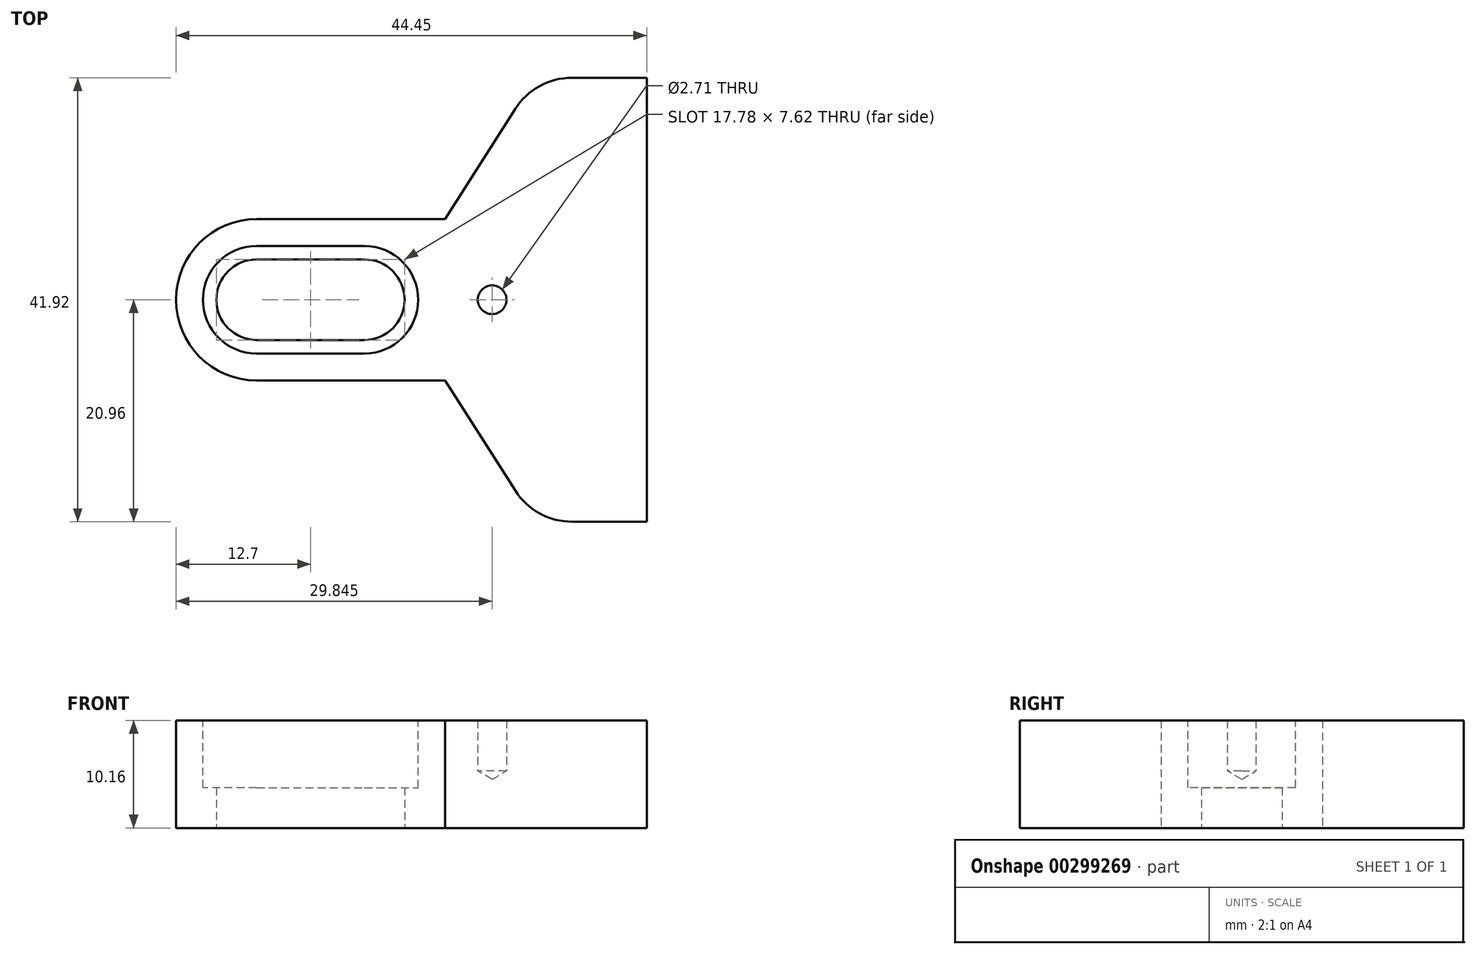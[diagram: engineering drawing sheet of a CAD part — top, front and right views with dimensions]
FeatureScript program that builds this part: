
annotation { "Feature Type Name" : "Feature", "Feature Type Description" : "" }
export const myFeature = defineFeature(function(context is Context, id is Id, definition is map)
    precondition{}
    {
        {
            var Q0;
            Q0=qCreatedBy(makeId("Top.planeOp"),FACE);
            var sketch = newSketch(context, id + "F0", { "sketchPlane" : qUnion([Q0])});
            skLineSegment(sketch, "E0.bottom", {"start": v(7.62, 7.62) * mm, "end": v(25.4, 7.62) * mm});
            skLineSegment(sketch, "E0.top", {"start": v(7.62, -7.62) * mm, "end": v(25.4, -7.62) * mm});
            skLineSegment(sketch, "E1", {"start": v(0, 0) * mm, "end": v(44.45, 0) * mm, "construction": true});
            skArc(sketch, "E2", {"start": v(7.62, 7.62) * mm, "mid": v(0, 0) * mm, "end": v(7.62, -7.62) * mm});
            skPoint(sketch, "E3.orphan", {"position": v(0, 7.62) * mm});
            skPoint(sketch, "E4.orphan", {"position": v(0, -7.62) * mm});
            skLineSegment(sketch, "E5", {"start": v(32.02, 18.02) * mm, "end": v(25.4, 7.62) * mm});
            skLineSegment(sketch, "E6", {"start": v(25.4, -7.62) * mm, "end": v(32.02, -18.02) * mm});
            skPoint(sketch, "E7.visualSharp", {"position": v(20.55, 0) * mm});
            skArc(sketch, "E8.filletArc", {"start": v(37.38, 20.96) * mm, "mid": v(34.32, 20.17) * mm, "end": v(32.02, 18.02) * mm});
            skArc(sketch, "E9.filletArc", {"start": v(32.02, -18.02) * mm, "mid": v(34.32, -20.17) * mm, "end": v(37.38, -20.96) * mm});
            skLineSegment(sketch, "E10", {"start": v(37.38, 20.96) * mm, "end": v(44.45, 20.96) * mm});
            skLineSegment(sketch, "E11", {"start": v(44.45, 20.96) * mm, "end": v(44.45, -20.96) * mm});
            skLineSegment(sketch, "E12", {"start": v(44.45, -20.96) * mm, "end": v(37.38, -20.96) * mm});
            skPoint(sketch, "E13.orphan", {"position": v(24.86, -6.78) * mm});
            skPoint(sketch, "E14.orphan", {"position": v(24.86, 6.78) * mm});
            skLineSegment(sketch, "E15", {"start": v(25.4, 7.62) * mm, "end": v(25.4, -7.62) * mm, "construction": true});
            skSolve(sketch);
        }
        {
            var Q0;
            Q0 = qSketchRegion(id + "F0", true);
            extrude(context, id + "F1", {"entities" : qUnion([Q0]), "depth" : 10.16 * mm});
        }
        {
            var Q0;
            Q0=makeQuery(id+"F1.opExtrude","CAP_FACE",FACE,{"disambiguationData":[OSD([sQuery(id+"F0.wireOp",EDGE,"E0.bottom"),sQuery(id+"F0.wireOp",EDGE,"E0.top"),sQuery(id+"F0.wireOp",EDGE,"E2"),sQuery(id+"F0.wireOp",EDGE,"E5"),sQuery(id+"F0.wireOp",EDGE,"E6"),sQuery(id+"F0.wireOp",EDGE,"E8.filletArc"),sQuery(id+"F0.wireOp",EDGE,"E9.filletArc"),sQuery(id+"F0.wireOp",EDGE,"E10"),sQuery(id+"F0.wireOp",EDGE,"E11"),sQuery(id+"F0.wireOp",EDGE,"E12")])],"isStart":false});
            var sketch = newSketch(context, id + "F2", { "sketchPlane" : qUnion([Q0])});
            skLineSegment(sketch, "E16", {"start": v(7.62, 0) * mm, "end": v(17.78, 0) * mm});
            skArc(sketch, "E17.0.startCap", {"start": v(7.62, -5.08) * mm, "mid": v(2.54, 0) * mm, "end": v(7.62, 5.08) * mm});
            skArc(sketch, "E17.0.endCap", {"start": v(17.78, 5.08) * mm, "mid": v(22.86, 0) * mm, "end": v(17.78, -5.08) * mm});
            skLineSegment(sketch, "E17.0.left", {"start": v(7.62, 5.08) * mm, "end": v(17.78, 5.08) * mm});
            skLineSegment(sketch, "E17.0.right", {"start": v(7.62, -5.08) * mm, "end": v(17.78, -5.08) * mm});
            skSolve(sketch);
        }
        {
            var Q0;
            Q0 = qSketchRegion(id + "F2", true);
            extrude(context, id + "F3", {"entities" : qUnion([Q0]), "operationType" : NewBodyOperationType.REMOVE, "oppositeDirection" : true, "depth" : 6.35 * mm, "offsetDistance" : 25.4 * mm});
        }
        {
            var Q0;
            Q0=qCreatedBy(makeId("Top.planeOp"),FACE);
            var sketch = newSketch(context, id + "F4", { "sketchPlane" : qUnion([Q0])});
            skLineSegment(sketch, "E18", {"start": v(7.62, 0) * mm, "end": v(17.78, 0) * mm});
            skArc(sketch, "E19.0.startCap", {"start": v(7.62, -3.81) * mm, "mid": v(3.81, 0) * mm, "end": v(7.62, 3.81) * mm});
            skArc(sketch, "E19.0.endCap", {"start": v(17.78, 3.81) * mm, "mid": v(21.6, 0) * mm, "end": v(17.78, -3.81) * mm});
            skLineSegment(sketch, "E19.0.left", {"start": v(7.62, 3.81) * mm, "end": v(17.78, 3.81) * mm});
            skLineSegment(sketch, "E19.0.right", {"start": v(7.62, -3.81) * mm, "end": v(17.78, -3.81) * mm});
            skSolve(sketch);
        }
        {
            var Q0;
            Q0 = qSketchRegion(id + "F4", true);
            extrude(context, id + "F5", {"entities" : qUnion([Q0]), "operationType" : NewBodyOperationType.REMOVE, "endBound" : BoundingType.THROUGH_ALL, "depth" : 25.4 * mm});
        }
        {
            var Q0;
            Q0=makeQuery(id+"F1.opExtrude","CAP_FACE",FACE,{"disambiguationData":[OSD([sQuery(id+"F0.wireOp",EDGE,"E0.bottom"),sQuery(id+"F0.wireOp",EDGE,"E0.top"),sQuery(id+"F0.wireOp",EDGE,"E2"),sQuery(id+"F0.wireOp",EDGE,"E5"),sQuery(id+"F0.wireOp",EDGE,"E6"),sQuery(id+"F0.wireOp",EDGE,"E8.filletArc"),sQuery(id+"F0.wireOp",EDGE,"E9.filletArc"),sQuery(id+"F0.wireOp",EDGE,"E10"),sQuery(id+"F0.wireOp",EDGE,"E11"),sQuery(id+"F0.wireOp",EDGE,"E12")])],"isStart":false});
            var sketch = newSketch(context, id + "F6", { "sketchPlane" : qUnion([Q0])});
            skPoint(sketch, "E20", {"position": v(29.85, 0) * mm});
            skSolve(sketch);
        }
        {
            var Q0;
            Q0=sQuery(id+"F6.wireOp",VERTEX,"E20");
            var Q1;
            Q1=makeQuery(id+"F1.opExtrude","SWEPT_BODY",BODY,{"disambiguationData":[OSD([sQuery(id+"F0.wireOp",EDGE,"E0.bottom"),sQuery(id+"F0.wireOp",EDGE,"E0.top"),sQuery(id+"F0.wireOp",EDGE,"E2"),sQuery(id+"F0.wireOp",EDGE,"E5"),sQuery(id+"F0.wireOp",EDGE,"E6"),sQuery(id+"F0.wireOp",EDGE,"E8.filletArc"),sQuery(id+"F0.wireOp",EDGE,"E9.filletArc"),sQuery(id+"F0.wireOp",EDGE,"E10"),sQuery(id+"F0.wireOp",EDGE,"E11"),sQuery(id+"F0.wireOp",EDGE,"E12")])]});
            hole(context, id + "F7", {"style" : HoleStyle.SIMPLE, "endStyle" : HoleEndStyle.BLIND, "standardTappedOrClearance" : lookupTablePath({ "standard" : "ANSI", "engagement" : "75%", "pitch" : "32 tpi", "size" : "#6", "type" : "Tapped" }), "standardBlindInLast" : lookupTablePath({ "standard" : "ANSI", "engagement" : "75%", "pitch" : "32 tpi", "size" : "#6", "type" : "Tapped" }), "holeDiameter" : 2.7 * mm, "showTappedDepth" : true, "holeDepth" : 4.77 * mm, "isTappedThrough" : true, "tappedDepth" : 2.4 * mm, "tapClearance" : 3, "startFromSketch" : true, "locations" : qUnion([Q0]), "scope" : qUnion([Q1]), "majorDiameter" : 3.5 * mm});
        }
    });
